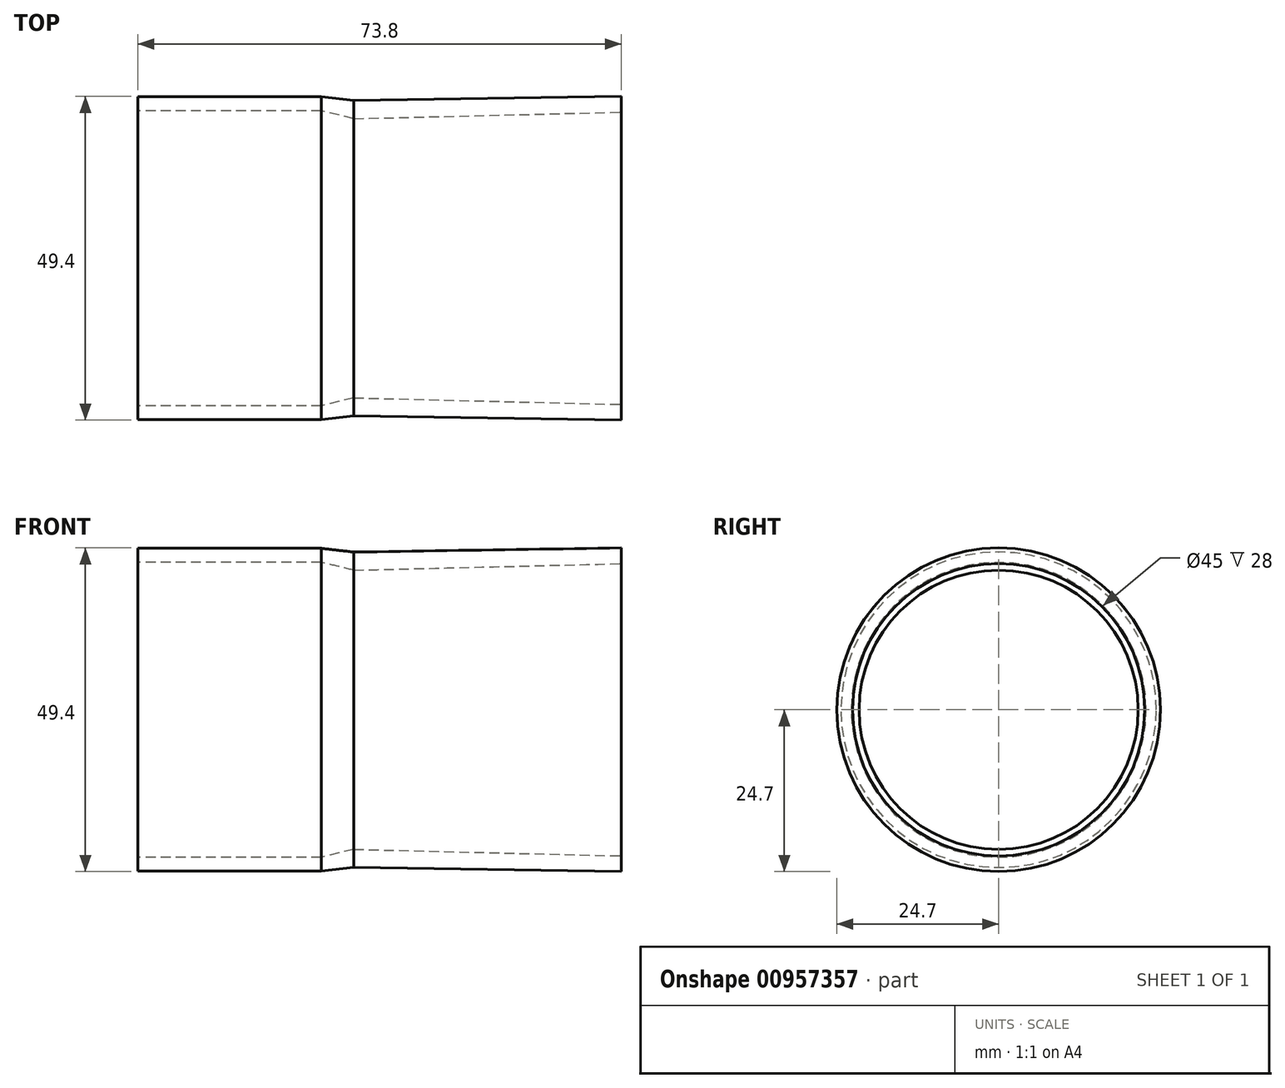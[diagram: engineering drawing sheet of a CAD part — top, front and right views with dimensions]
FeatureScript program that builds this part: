
annotation { "Feature Type Name" : "Feature", "Feature Type Description" : "" }
export const myFeature = defineFeature(function(context is Context, id is Id, definition is map)
    precondition{}
    {
        {
            var Q0;
            Q0=qCreatedBy(makeId("Top.planeOp"),FACE);
            var sketch = newSketch(context, id + "F0", { "sketchPlane" : qUnion([Q0])});
            skLineSegment(sketch, "E0", {"start": v(3.5, 21.3) * mm, "end": v(-1.47, 22.5) * mm});
            skLineSegment(sketch, "E1", {"start": v(-1.47, 22.5) * mm, "end": v(-29.47, 22.5) * mm});
            skLineSegment(sketch, "E2", {"start": v(-29.47, 22.5) * mm, "end": v(-29.47, 24.63) * mm});
            skLineSegment(sketch, "E3", {"start": v(-29.47, 24.63) * mm, "end": v(-1.47, 24.63) * mm});
            skLineSegment(sketch, "E4", {"start": v(-1.47, 24.63) * mm, "end": v(3.5, 24.07) * mm});
            skLineSegment(sketch, "E5", {"start": v(-43.34, 0) * mm, "end": v(39.1, 0) * mm, "construction": true});
            skPoint(sketch, "E6", {"position": v(-31.2, 22.5) * mm});
            skLineSegment(sketch, "E7", {"start": v(-31.2, 22.5) * mm, "end": v(-31.2, 0) * mm, "construction": true});
            skLineSegment(sketch, "E8", {"start": v(3.5, 24.07) * mm, "end": v(44.29, 24.7) * mm});
            skLineSegment(sketch, "E9", {"start": v(44.29, 24.7) * mm, "end": v(44.33, 22.3) * mm});
            skLineSegment(sketch, "E10", {"start": v(44.33, 22.3) * mm, "end": v(3.5, 21.3) * mm});
            skPoint(sketch, "E11", {"position": v(44.33, 22.3) * mm});
            skPoint(sketch, "E12", {"position": v(23.9, 21.8) * mm});
            skPoint(sketch, "E13", {"position": v(3.5, 21.3) * mm});
            skLineSegment(sketch, "E14", {"start": v(44.33, 22.3) * mm, "end": v(44.33, 0) * mm, "construction": true});
            skLineSegment(sketch, "E15", {"start": v(3.5, 21.3) * mm, "end": v(3.5, 0) * mm, "construction": true});
            skSolve(sketch);
        }
        {
            var Q0;
            Q0=makeQuery(id+"F0.imprint","IMPRINT",FACE,{"disambiguationData":[TD([[makeQuery(id+"F0.imprint","IMPRINT",EDGE,{"derivedFrom":sQuery(id+"F0.wireOp",EDGE,"E0")}),-1.0]])]});
            var Q1;
            Q1=sQuery(id+"F0.wireOp",EDGE,"E5");
            revolve(context, id + "F1", {"surfaceOperationType" : NewSurfaceOperationType.NEW, "entities" : qUnion([Q0]), "axis" : qUnion([Q1]), "revolveType" : RevolveType.FULL});
        }
    });
